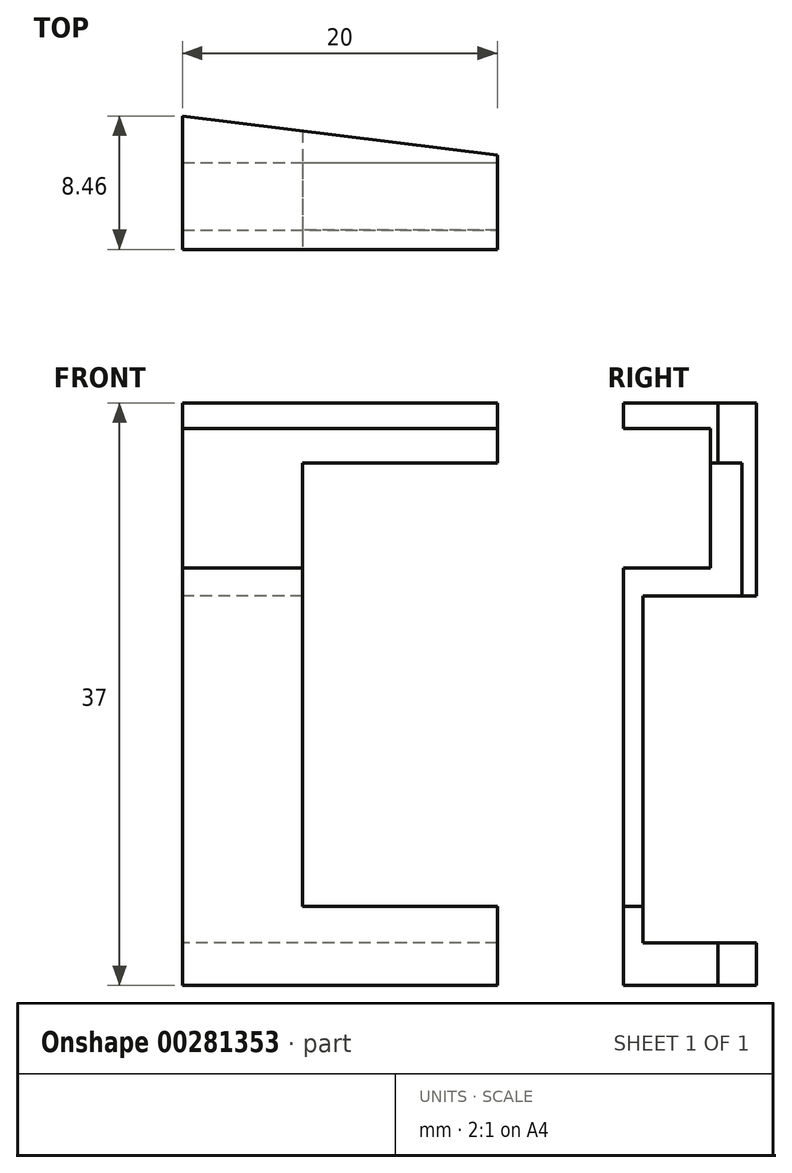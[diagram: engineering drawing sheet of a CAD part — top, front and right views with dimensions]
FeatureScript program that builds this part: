
annotation { "Feature Type Name" : "Feature", "Feature Type Description" : "" }
export const myFeature = defineFeature(function(context is Context, id is Id, definition is map)
    precondition{}
    {
        {
            var Q0;
            Q0=qCreatedBy(makeId("Top.planeOp"),FACE);
            var sketch = newSketch(context, id + "F0", { "sketchPlane" : qUnion([Q0])});
            skLineSegment(sketch, "E0.bottom", {"start": v(10.44, 3) * mm, "end": v(-9.56, 3) * mm});
            skLineSegment(sketch, "E0.top", {"start": v(10.44, -3) * mm, "end": v(-9.56, -3) * mm});
            skLineSegment(sketch, "E0.left", {"start": v(10.44, 3) * mm, "end": v(10.44, -3) * mm});
            skLineSegment(sketch, "E0.right", {"start": v(-9.56, 3) * mm, "end": v(-9.56, -3) * mm});
            skPoint(sketch, "E0.middle", {"position": v(0.44, 0) * mm});
            skLineSegment(sketch, "E1", {"start": v(10.44, 3) * mm, "end": v(-9.56, 5.46) * mm});
            skLineSegment(sketch, "E2", {"start": v(-9.56, 5.46) * mm, "end": v(-9.56, 3) * mm});
            skSolve(sketch);
        }
        {
            var Q0;
            Q0 = qSketchRegion(id + "F0", true);
            extrude(context, id + "F1", {"entities" : qUnion([Q0]), "depth" : 37 * mm});
        }
        {
            var Q0;
            Q0=qCreatedBy(makeId("Right.planeOp"),FACE);
            var sketch = newSketch(context, id + "F2", { "sketchPlane" : qUnion([Q0])});
            skLineSegment(sketch, "E3.bottom", {"start": v(11.81, 24.73) * mm, "end": v(-1.76, 24.73) * mm});
            skLineSegment(sketch, "E3.top", {"start": v(11.81, 2.7) * mm, "end": v(-1.76, 2.7) * mm});
            skLineSegment(sketch, "E3.left", {"start": v(11.81, 24.73) * mm, "end": v(11.81, 2.7) * mm});
            skLineSegment(sketch, "E3.right", {"start": v(-1.76, 24.73) * mm, "end": v(-1.76, 2.7) * mm});
            skLineSegment(sketch, "E4.bottom", {"start": v(2.52, 26.51) * mm, "end": v(-6.38, 26.51) * mm});
            skLineSegment(sketch, "E4.top", {"start": v(2.52, 35.38) * mm, "end": v(-6.38, 35.38) * mm});
            skLineSegment(sketch, "E4.left", {"start": v(2.52, 26.51) * mm, "end": v(2.52, 35.38) * mm});
            skLineSegment(sketch, "E4.right", {"start": v(-6.38, 26.51) * mm, "end": v(-6.38, 35.38) * mm});
            skSolve(sketch);
        }
        {
            var Q0;
            Q0 = qSketchRegion(id + "F2", true);
            extrude(context, id + "F3", {"entities" : qUnion([Q0]), "operationType" : NewBodyOperationType.REMOVE, "endBound" : BoundingType.SYMMETRIC, "oppositeDirection" : true, "depth" : 25 * mm});
        }
        {
            var Q0;
            Q0=qCreatedBy(makeId("Front.planeOp"),FACE);
            var sketch = newSketch(context, id + "F4", { "sketchPlane" : qUnion([Q0])});
            skLineSegment(sketch, "E5.bottom", {"start": v(20.74, 33.16) * mm, "end": v(-1.93, 33.16) * mm});
            skLineSegment(sketch, "E5.top", {"start": v(20.74, 5.01) * mm, "end": v(-1.93, 5.01) * mm});
            skLineSegment(sketch, "E5.left", {"start": v(20.74, 33.16) * mm, "end": v(20.74, 5.01) * mm});
            skLineSegment(sketch, "E5.right", {"start": v(-1.93, 33.16) * mm, "end": v(-1.93, 5.01) * mm});
            skSolve(sketch);
        }
        {
            var Q0;
            Q0 = qSketchRegion(id + "F4", true);
            extrude(context, id + "F5", {"entities" : qUnion([Q0]), "operationType" : NewBodyOperationType.REMOVE, "endBound" : BoundingType.SYMMETRIC, "oppositeDirection" : true, "depth" : 25 * mm});
        }
    });
